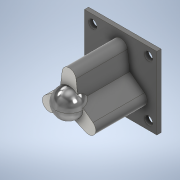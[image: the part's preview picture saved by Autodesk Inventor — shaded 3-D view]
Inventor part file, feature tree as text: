
AUTODESK INVENTOR PART (.ipt)
format: ipt  version: 2022 (Build 260153000, 153)  size: 244,736 bytes
history: native  units: mm
features: other x3, sketch x3, extrude x2, pattern_circular x1, hole x1
ambient origin geometry x8: Origin, YZ Plane, XZ Plane, XY Plane, X Axis, Y Axis, Z Axis, Center Point
bodies: Body1 (feature_tree)
feature tree (10):
  other  "フォーム1"
  other  "作業平面1"
  extrude  "押し出し1"  [1 undecoded]
  extrude  "押し出し2"  Depth=26.0mm
  pattern_circular  "円形状パターン1"  [2 undecoded]
  hole  "穴1"  [1 undecoded]
  sketch  "スケッチ2"
  sketch  "スケッチ3"
  sketch  "スケッチ4"
  other  "ソリッド1"
note: 4 required parameter values undecoded (feature->parameter linkage not recoverable at this tier; creation-order binding heuristic only, values carry confidence <= 0.55)
